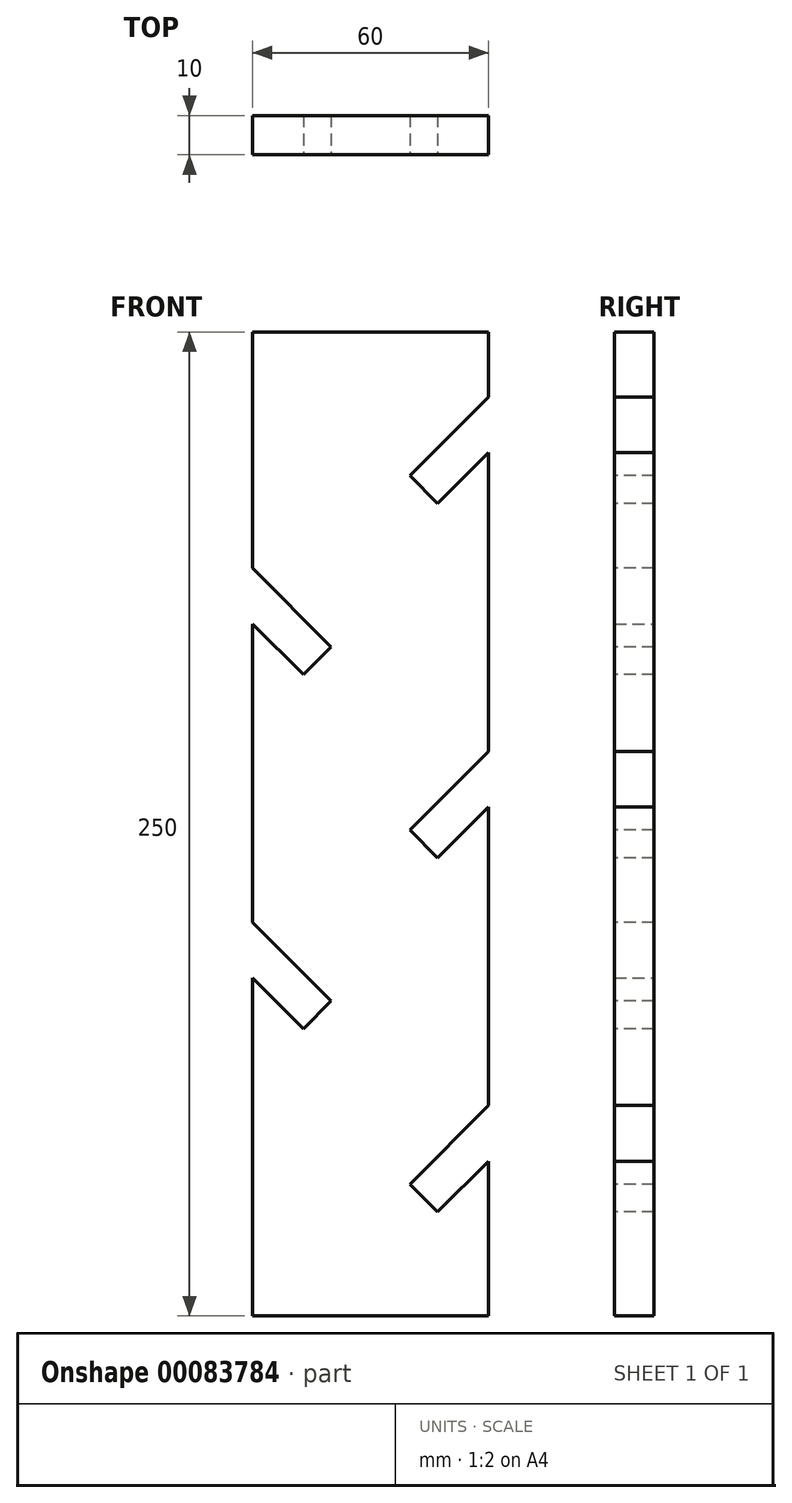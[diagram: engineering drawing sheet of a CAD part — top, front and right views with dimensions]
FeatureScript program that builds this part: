
annotation { "Feature Type Name" : "Feature", "Feature Type Description" : "" }
export const myFeature = defineFeature(function(context is Context, id is Id, definition is map)
    precondition{}
    {
        {
            var Q0;
            Q0=qCreatedBy(makeId("Front.planeOp"),FACE);
            var sketch = newSketch(context, id + "F0", { "sketchPlane" : qUnion([Q0])});
            skLineSegment(sketch, "E0.bottom", {"start": v(-30, 125) * mm, "end": v(30, 125) * mm});
            skLineSegment(sketch, "E0.top", {"start": v(-30, -125) * mm, "end": v(30, -125) * mm});
            skLineSegment(sketch, "E0.left", {"start": v(-30, 125) * mm, "end": v(-30, -125) * mm});
            skLineSegment(sketch, "E0.right", {"start": v(30, 125) * mm, "end": v(30, -125) * mm});
            skPoint(sketch, "E0.middle", {"position": v(0, 0) * mm});
            skSolve(sketch);
        }
        {
            var Q0;
            Q0=makeQuery(id+"F0.imprint","IMPRINT",FACE,{"disambiguationData":[TD([[makeQuery(id+"F0.imprint","IMPRINT",EDGE,{"derivedFrom":sQuery(id+"F0.wireOp",EDGE,"E0.bottom")}),-1.0]])]});
            extrude(context, id + "F1", {"entities" : qUnion([Q0]), "depth" : 10 * mm});
        }
        {
            var Q0;
            Q0=makeQuery(id+"F1.opExtrude","CAP_FACE",FACE,{"disambiguationData":[OSD([sQuery(id+"F0.wireOp",EDGE,"E0.bottom"),sQuery(id+"F0.wireOp",EDGE,"E0.top"),sQuery(id+"F0.wireOp",EDGE,"E0.left"),sQuery(id+"F0.wireOp",EDGE,"E0.right")])],"isStart":false});
            var sketch = newSketch(context, id + "F2", { "sketchPlane" : qUnion([Q0])});
            skLineSegment(sketch, "E1", {"start": v(10, 125) * mm, "end": v(10, -125) * mm, "construction": true});
            skLineSegment(sketch, "E2", {"start": v(10, 88.47) * mm, "end": v(98.39, 176.86) * mm});
            skLineSegment(sketch, "E3", {"start": v(98.39, 176.86) * mm, "end": v(105.46, 169.79) * mm});
            skLineSegment(sketch, "E4", {"start": v(105.46, 169.79) * mm, "end": v(17.07, 81.4) * mm});
            skLineSegment(sketch, "E5", {"start": v(17.07, 81.4) * mm, "end": v(10, 88.47) * mm});
            skLineSegment(sketch, "E6", {"start": v(-30, 88.47) * mm, "end": v(30, 88.47) * mm, "construction": true});
            skLineSegment(sketch, "E7.0.1.0", {"start": v(-30, -1.53) * mm, "end": v(30, -1.53) * mm, "construction": true});
            skLineSegment(sketch, "E7.0.1.1", {"start": v(105.46, 79.79) * mm, "end": v(17.07, -8.6) * mm});
            skLineSegment(sketch, "E7.0.1.2", {"start": v(10, -1.53) * mm, "end": v(98.39, 86.86) * mm});
            skLineSegment(sketch, "E7.0.1.3", {"start": v(17.07, -8.6) * mm, "end": v(10, -1.53) * mm});
            skLineSegment(sketch, "E7.0.1.4", {"start": v(98.39, 86.86) * mm, "end": v(105.46, 79.79) * mm});
            skLineSegment(sketch, "E7.0.2.0", {"start": v(-30, -91.53) * mm, "end": v(30, -91.53) * mm, "construction": true});
            skLineSegment(sketch, "E7.0.2.1", {"start": v(105.46, -10.21) * mm, "end": v(17.07, -98.6) * mm});
            skLineSegment(sketch, "E7.0.2.2", {"start": v(10, -91.53) * mm, "end": v(98.39, -3.14) * mm});
            skLineSegment(sketch, "E7.0.2.3", {"start": v(17.07, -98.6) * mm, "end": v(10, -91.53) * mm});
            skLineSegment(sketch, "E7.0.2.4", {"start": v(98.39, -3.14) * mm, "end": v(105.46, -10.21) * mm});
            skLineSegment(sketch, "E7.direction1", {"start": v(-30, 88.47) * mm, "end": v(-30.52, 88.47) * mm, "construction": true});
            skLineSegment(sketch, "E7.direction2", {"start": v(-30, 88.47) * mm, "end": v(-30, -1.53) * mm, "construction": true});
            skLineSegment(sketch, "E8", {"start": v(-30, 45) * mm, "end": v(30, 45) * mm, "construction": true});
            skLineSegment(sketch, "E9", {"start": v(-10, 125) * mm, "end": v(-10, -125) * mm, "construction": true});
            skLineSegment(sketch, "E10", {"start": v(-10, 45) * mm, "end": v(-98.39, 133.39) * mm});
            skLineSegment(sketch, "E11", {"start": v(-98.39, 133.39) * mm, "end": v(-105.46, 126.32) * mm});
            skLineSegment(sketch, "E12", {"start": v(-105.46, 126.32) * mm, "end": v(-17.07, 37.93) * mm});
            skLineSegment(sketch, "E13", {"start": v(-17.07, 37.93) * mm, "end": v(-10, 45) * mm});
            skLineSegment(sketch, "E14.0.1.0", {"start": v(-30, -1.53) * mm, "end": v(-30, -91.53) * mm, "construction": true});
            skLineSegment(sketch, "E14.0.1.1", {"start": v(-10, -45) * mm, "end": v(-98.39, 43.39) * mm});
            skLineSegment(sketch, "E14.0.1.2", {"start": v(-105.46, 36.32) * mm, "end": v(-17.07, -52.07) * mm});
            skLineSegment(sketch, "E14.0.1.3", {"start": v(-98.39, 43.39) * mm, "end": v(-105.46, 36.32) * mm});
            skLineSegment(sketch, "E14.0.1.4", {"start": v(-17.07, -52.07) * mm, "end": v(-10, -45) * mm});
            skLineSegment(sketch, "E14.0.1.5", {"start": v(-30, -45) * mm, "end": v(30, -45) * mm, "construction": true});
            skLineSegment(sketch, "E14.direction2", {"start": v(-30, -1.53) * mm, "end": v(-30, -91.53) * mm, "construction": true});
            skSolve(sketch);
        }
        {
            var Q0;
            Q0 = qSketchRegion(id + "F2", true);
            extrude(context, id + "F3", {"entities" : qUnion([Q0]), "operationType" : NewBodyOperationType.REMOVE, "oppositeDirection" : true, "depth" : 10 * mm});
        }
    });
